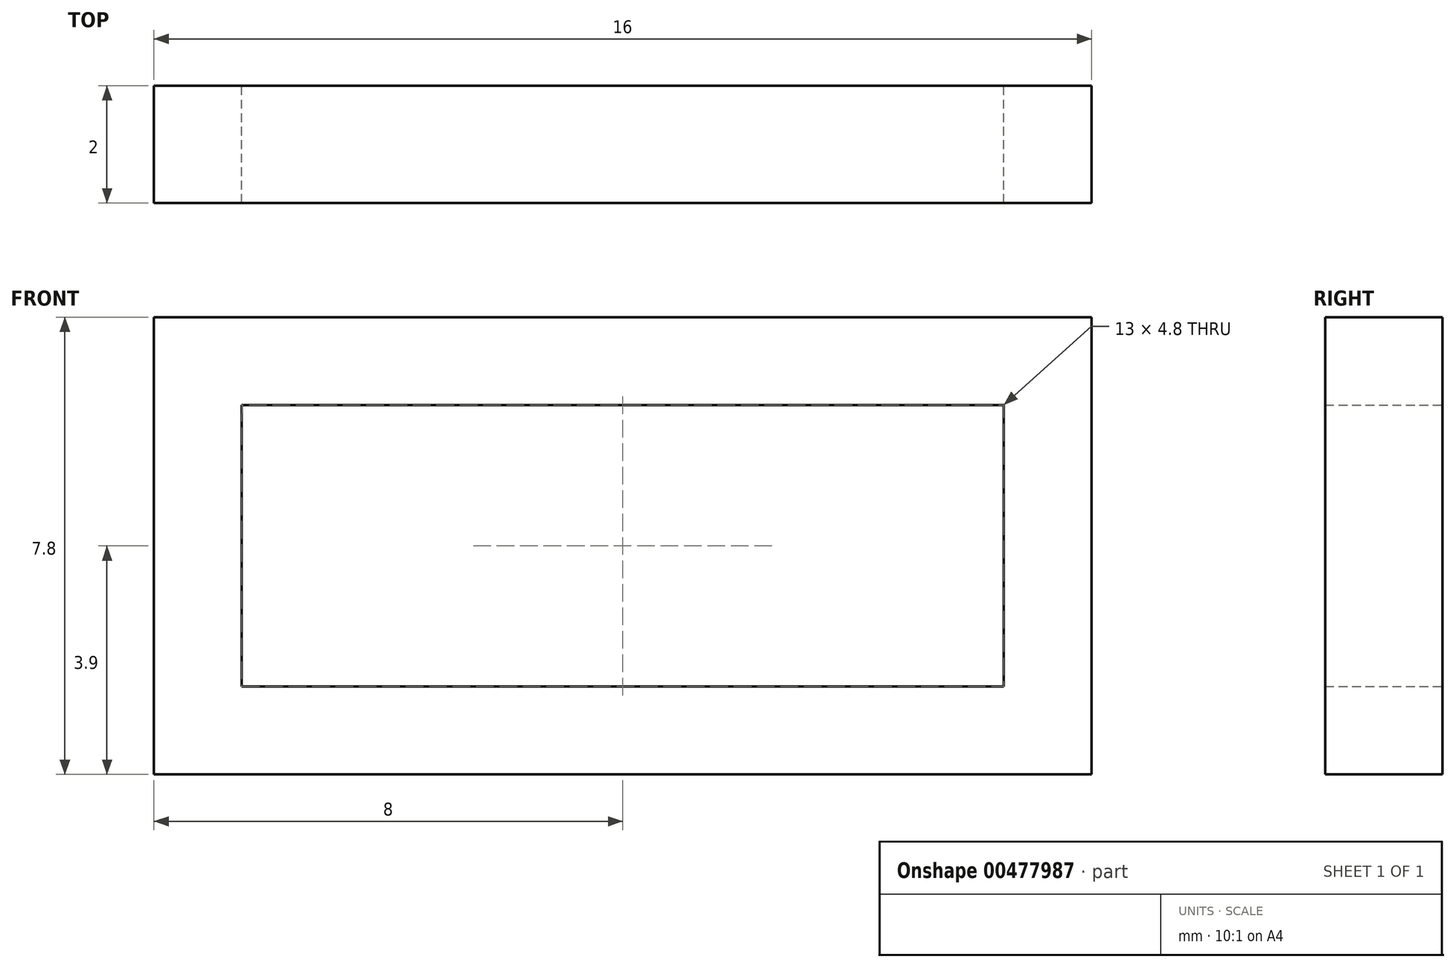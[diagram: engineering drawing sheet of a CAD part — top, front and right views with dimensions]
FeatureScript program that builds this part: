
annotation { "Feature Type Name" : "Feature", "Feature Type Description" : "" }
export const myFeature = defineFeature(function(context is Context, id is Id, definition is map)
    precondition{}
    {
        {
            var Q0;
            Q0=qCreatedBy(makeId("Front.planeOp"),FACE);
            var sketch = newSketch(context, id + "F0", { "sketchPlane" : qUnion([Q0])});
            skLineSegment(sketch, "E0.bottom", {"start": v(8, 3.9) * mm, "end": v(-8, 3.9) * mm});
            skLineSegment(sketch, "E0.top", {"start": v(8, -3.9) * mm, "end": v(-8, -3.9) * mm});
            skLineSegment(sketch, "E0.left", {"start": v(8, 3.9) * mm, "end": v(8, -3.9) * mm});
            skLineSegment(sketch, "E0.right", {"start": v(-8, 3.9) * mm, "end": v(-8, -3.9) * mm});
            skPoint(sketch, "E0.middle", {"position": v(0, 0) * mm});
            skLineSegment(sketch, "E1.0", {"start": v(8, 2.4) * mm, "end": v(-8, 2.4) * mm});
            skLineSegment(sketch, "E2.0", {"start": v(-6.5, 3.9) * mm, "end": v(-6.5, -3.9) * mm});
            skLineSegment(sketch, "E3.0", {"start": v(8, -2.4) * mm, "end": v(-8, -2.4) * mm});
            skLineSegment(sketch, "E4.0", {"start": v(6.5, 3.9) * mm, "end": v(6.5, -3.9) * mm});
            skSolve(sketch);
        }
        {
            var Q0;
            Q0 = qSketchRegion(id + "F0", true);
            extrude(context, id + "F1", {"entities" : qUnion([Q0]), "depth" : 2 * mm});
        }
    });
